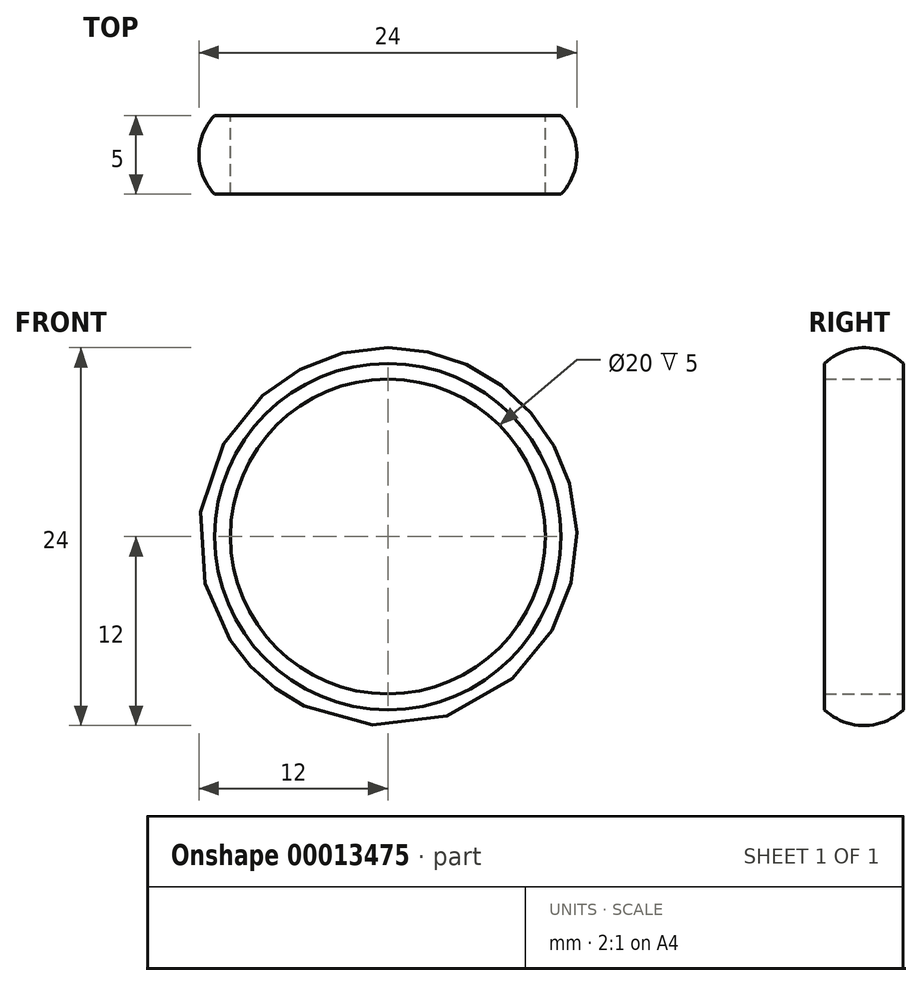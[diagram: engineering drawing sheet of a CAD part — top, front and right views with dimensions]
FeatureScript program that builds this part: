
annotation { "Feature Type Name" : "Feature", "Feature Type Description" : "" }
export const myFeature = defineFeature(function(context is Context, id is Id, definition is map)
    precondition{}
    {
        {
            var Q0;
            Q0=qCreatedBy(makeId("Front.planeOp"),FACE);
            var sketch = newSketch(context, id + "F0", { "sketchPlane" : qUnion([Q0])});
            skCircle(sketch, "E0", {"center": v(0, 0) * mm, "radius": 10 * mm, "construction": true});
            skSolve(sketch);
        }
        {
            var Q0;
            Q0=qCreatedBy(makeId("Right.planeOp"),FACE);
            var sketch = newSketch(context, id + "F1", { "sketchPlane" : qUnion([Q0])});
            skLineSegment(sketch, "E1.0", {"start": v(0, -10) * mm, "end": v(0, 10) * mm, "construction": true});
            skLineSegment(sketch, "E2", {"start": v(-2.5, 10) * mm, "end": v(2.5, 10) * mm});
            skLineSegment(sketch, "E3", {"start": v(2.5, 10) * mm, "end": v(2.5, 11) * mm});
            skLineSegment(sketch, "E4", {"start": v(-2.5, 11) * mm, "end": v(-2.5, 10) * mm});
            skLineSegment(sketch, "E5", {"start": v(0, 12) * mm, "end": v(0, 10) * mm, "construction": true});
            skLineSegment(sketch, "E6.0", {"start": v(2.5, 11) * mm, "end": v(-2.5, 11) * mm, "construction": true});
            skArc(sketch, "E7", {"start": v(2.5, 11) * mm, "mid": v(0, 12) * mm, "end": v(-2.5, 11) * mm});
            skPoint(sketch, "E8.orphan", {"position": v(2.5, 12) * mm});
            skPoint(sketch, "E9.orphan", {"position": v(-2.5, 12) * mm});
            skSolve(sketch);
        }
        {
            var Q0;
            Q0 = qSketchRegion(id + "F1", true);
            var Q1;
            Q1=sQuery(id+"F0.wireOp",EDGE,"E0");
            revolve(context, id + "F2", {"entities" : qUnion([Q0]), "axis" : qUnion([Q1]), "revolveType" : RevolveType.FULL});
        }
    });
